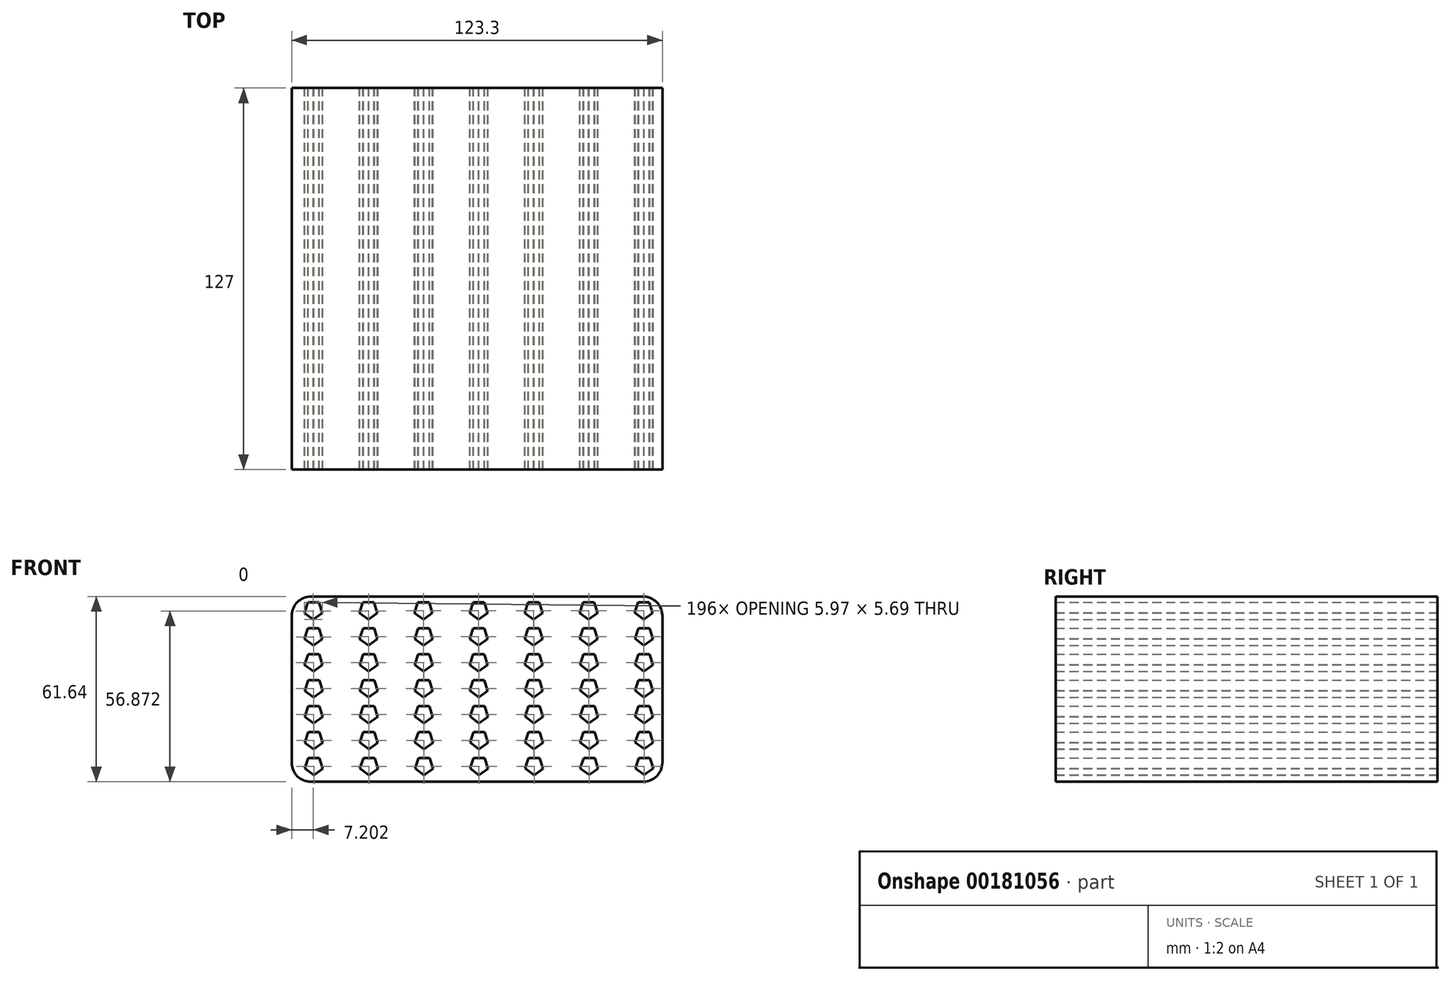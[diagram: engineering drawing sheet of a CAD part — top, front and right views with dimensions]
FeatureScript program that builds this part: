
annotation { "Feature Type Name" : "Feature", "Feature Type Description" : "" }
export const myFeature = defineFeature(function(context is Context, id is Id, definition is map)
    precondition{}
    {
        {
            var Q0;
            Q0=qCreatedBy(makeId("Front.planeOp"),FACE);
            var sketch = newSketch(context, id + "F0", { "sketchPlane" : qUnion([Q0])});
            skLineSegment(sketch, "E0.bottom", {"start": v(55.3, 30.82) * mm, "end": v(-55.3, 30.82) * mm});
            skLineSegment(sketch, "E0.top", {"start": v(55.3, -30.82) * mm, "end": v(-55.3, -30.82) * mm});
            skLineSegment(sketch, "E0.left", {"start": v(61.65, 24.47) * mm, "end": v(61.65, -24.47) * mm});
            skLineSegment(sketch, "E0.right", {"start": v(-61.65, 24.47) * mm, "end": v(-61.65, -24.47) * mm});
            skPoint(sketch, "E0.middle", {"position": v(0, 0) * mm});
            skCircle(sketch, "E1.cCircle", {"center": v(-54.44, 26.35) * mm, "radius": 2.54 * mm, "construction": true});
            skLineSegment(sketch, "E1.0", {"start": v(-52.58, 28.87) * mm, "end": v(-51.46, 25.36) * mm});
            skLineSegment(sketch, "E1.1", {"start": v(-51.46, 25.36) * mm, "end": v(-54.46, 23.2) * mm});
            skLineSegment(sketch, "E1.2", {"start": v(-54.46, 23.2) * mm, "end": v(-57.43, 25.4) * mm});
            skLineSegment(sketch, "E1.3", {"start": v(-57.43, 25.4) * mm, "end": v(-56.27, 28.9) * mm});
            skLineSegment(sketch, "E1.4", {"start": v(-56.27, 28.9) * mm, "end": v(-52.58, 28.87) * mm});
            skPoint(sketch, "E1.0.midPoint", {"position": v(-52.02, 27.12) * mm});
            skPoint(sketch, "E2.0.1.0", {"position": v(-52, 18.49) * mm});
            skLineSegment(sketch, "E2.0.1.1", {"start": v(-56.24, 20.27) * mm, "end": v(-52.55, 20.24) * mm});
            skLineSegment(sketch, "E2.0.1.2", {"start": v(-51.43, 16.73) * mm, "end": v(-54.43, 14.58) * mm});
            skLineSegment(sketch, "E2.0.1.3", {"start": v(-57.4, 16.76) * mm, "end": v(-56.24, 20.27) * mm});
            skLineSegment(sketch, "E2.0.1.4", {"start": v(-54.43, 14.58) * mm, "end": v(-57.4, 16.76) * mm});
            skLineSegment(sketch, "E2.0.1.5", {"start": v(-52.55, 20.24) * mm, "end": v(-51.43, 16.73) * mm});
            skCircle(sketch, "E2.0.1.6", {"center": v(-54.41, 17.72) * mm, "radius": 2.54 * mm, "construction": true});
            skPoint(sketch, "E2.0.2.0", {"position": v(-51.96, 9.86) * mm});
            skLineSegment(sketch, "E2.0.2.1", {"start": v(-56.21, 11.64) * mm, "end": v(-52.52, 11.61) * mm});
            skLineSegment(sketch, "E2.0.2.2", {"start": v(-51.4, 8.1) * mm, "end": v(-54.4, 5.95) * mm});
            skLineSegment(sketch, "E2.0.2.3", {"start": v(-57.37, 8.13) * mm, "end": v(-56.21, 11.64) * mm});
            skLineSegment(sketch, "E2.0.2.4", {"start": v(-54.4, 5.95) * mm, "end": v(-57.37, 8.13) * mm});
            skLineSegment(sketch, "E2.0.2.5", {"start": v(-52.52, 11.61) * mm, "end": v(-51.4, 8.1) * mm});
            skCircle(sketch, "E2.0.2.6", {"center": v(-54.38, 9.09) * mm, "radius": 2.54 * mm, "construction": true});
            skPoint(sketch, "E2.0.3.0", {"position": v(-51.93, 1.23) * mm});
            skLineSegment(sketch, "E2.0.3.1", {"start": v(-56.18, 3) * mm, "end": v(-52.5, 2.98) * mm});
            skLineSegment(sketch, "E2.0.3.2", {"start": v(-51.37, -0.53) * mm, "end": v(-54.37, -2.68) * mm});
            skLineSegment(sketch, "E2.0.3.3", {"start": v(-57.34, -0.5) * mm, "end": v(-56.18, 3) * mm});
            skLineSegment(sketch, "E2.0.3.4", {"start": v(-54.37, -2.68) * mm, "end": v(-57.34, -0.5) * mm});
            skLineSegment(sketch, "E2.0.3.5", {"start": v(-52.5, 2.98) * mm, "end": v(-51.37, -0.53) * mm});
            skCircle(sketch, "E2.0.3.6", {"center": v(-54.35, 0.46) * mm, "radius": 2.54 * mm, "construction": true});
            skPoint(sketch, "E2.0.4.0", {"position": v(-51.9, -7.4) * mm});
            skLineSegment(sketch, "E2.0.4.1", {"start": v(-56.15, -5.62) * mm, "end": v(-52.46, -5.65) * mm});
            skLineSegment(sketch, "E2.0.4.2", {"start": v(-51.34, -9.16) * mm, "end": v(-54.34, -11.31) * mm});
            skLineSegment(sketch, "E2.0.4.3", {"start": v(-57.31, -9.13) * mm, "end": v(-56.15, -5.62) * mm});
            skLineSegment(sketch, "E2.0.4.4", {"start": v(-54.34, -11.31) * mm, "end": v(-57.31, -9.13) * mm});
            skLineSegment(sketch, "E2.0.4.5", {"start": v(-52.46, -5.65) * mm, "end": v(-51.34, -9.16) * mm});
            skCircle(sketch, "E2.0.4.6", {"center": v(-54.32, -8.17) * mm, "radius": 2.54 * mm, "construction": true});
            skPoint(sketch, "E2.0.5.0", {"position": v(-51.87, -16.03) * mm});
            skLineSegment(sketch, "E2.0.5.1", {"start": v(-56.12, -14.25) * mm, "end": v(-52.43, -14.28) * mm});
            skLineSegment(sketch, "E2.0.5.2", {"start": v(-51.31, -17.8) * mm, "end": v(-54.31, -19.94) * mm});
            skLineSegment(sketch, "E2.0.5.3", {"start": v(-57.29, -17.76) * mm, "end": v(-56.12, -14.25) * mm});
            skLineSegment(sketch, "E2.0.5.4", {"start": v(-54.31, -19.94) * mm, "end": v(-57.29, -17.76) * mm});
            skLineSegment(sketch, "E2.0.5.5", {"start": v(-52.43, -14.28) * mm, "end": v(-51.31, -17.8) * mm});
            skCircle(sketch, "E2.0.5.6", {"center": v(-54.3, -16.8) * mm, "radius": 2.54 * mm, "construction": true});
            skPoint(sketch, "E2.0.6.0", {"position": v(-51.84, -24.67) * mm});
            skLineSegment(sketch, "E2.0.6.1", {"start": v(-56.1, -22.88) * mm, "end": v(-52.4, -22.9) * mm});
            skLineSegment(sketch, "E2.0.6.2", {"start": v(-51.28, -26.42) * mm, "end": v(-54.28, -28.57) * mm});
            skLineSegment(sketch, "E2.0.6.3", {"start": v(-57.26, -26.39) * mm, "end": v(-56.1, -22.88) * mm});
            skLineSegment(sketch, "E2.0.6.4", {"start": v(-54.28, -28.57) * mm, "end": v(-57.26, -26.39) * mm});
            skLineSegment(sketch, "E2.0.6.5", {"start": v(-52.4, -22.9) * mm, "end": v(-51.28, -26.42) * mm});
            skCircle(sketch, "E2.0.6.6", {"center": v(-54.26, -25.44) * mm, "radius": 2.54 * mm, "construction": true});
            skPoint(sketch, "E2.1.0.0", {"position": v(-33.7, 27.12) * mm});
            skLineSegment(sketch, "E2.1.0.1", {"start": v(-37.95, 28.9) * mm, "end": v(-34.26, 28.88) * mm});
            skLineSegment(sketch, "E2.1.0.2", {"start": v(-33.14, 25.36) * mm, "end": v(-36.14, 23.21) * mm});
            skLineSegment(sketch, "E2.1.0.3", {"start": v(-39.12, 25.4) * mm, "end": v(-37.95, 28.9) * mm});
            skLineSegment(sketch, "E2.1.0.4", {"start": v(-36.14, 23.21) * mm, "end": v(-39.12, 25.4) * mm});
            skLineSegment(sketch, "E2.1.0.5", {"start": v(-34.26, 28.88) * mm, "end": v(-33.14, 25.36) * mm});
            skCircle(sketch, "E2.1.0.6", {"center": v(-36.12, 26.35) * mm, "radius": 2.54 * mm, "construction": true});
            skPoint(sketch, "E2.1.1.0", {"position": v(-33.67, 18.5) * mm});
            skLineSegment(sketch, "E2.1.1.1", {"start": v(-37.92, 20.27) * mm, "end": v(-34.23, 20.25) * mm});
            skLineSegment(sketch, "E2.1.1.2", {"start": v(-33.11, 16.73) * mm, "end": v(-36.11, 14.58) * mm});
            skLineSegment(sketch, "E2.1.1.3", {"start": v(-39.09, 16.77) * mm, "end": v(-37.92, 20.27) * mm});
            skLineSegment(sketch, "E2.1.1.4", {"start": v(-36.11, 14.58) * mm, "end": v(-39.09, 16.77) * mm});
            skLineSegment(sketch, "E2.1.1.5", {"start": v(-34.23, 20.25) * mm, "end": v(-33.11, 16.73) * mm});
            skCircle(sketch, "E2.1.1.6", {"center": v(-36.1, 17.72) * mm, "radius": 2.54 * mm, "construction": true});
            skPoint(sketch, "E2.1.2.0", {"position": v(-33.64, 9.86) * mm});
            skLineSegment(sketch, "E2.1.2.1", {"start": v(-37.9, 11.64) * mm, "end": v(-34.2, 11.62) * mm});
            skLineSegment(sketch, "E2.1.2.2", {"start": v(-33.08, 8.1) * mm, "end": v(-36.08, 5.95) * mm});
            skLineSegment(sketch, "E2.1.2.3", {"start": v(-39.06, 8.14) * mm, "end": v(-37.9, 11.64) * mm});
            skLineSegment(sketch, "E2.1.2.4", {"start": v(-36.08, 5.95) * mm, "end": v(-39.06, 8.14) * mm});
            skLineSegment(sketch, "E2.1.2.5", {"start": v(-34.2, 11.62) * mm, "end": v(-33.08, 8.1) * mm});
            skCircle(sketch, "E2.1.2.6", {"center": v(-36.06, 9.1) * mm, "radius": 2.54 * mm, "construction": true});
            skPoint(sketch, "E2.1.3.0", {"position": v(-33.61, 1.23) * mm});
            skLineSegment(sketch, "E2.1.3.1", {"start": v(-37.86, 3.01) * mm, "end": v(-34.17, 2.99) * mm});
            skLineSegment(sketch, "E2.1.3.2", {"start": v(-33.06, -0.53) * mm, "end": v(-36.05, -2.68) * mm});
            skLineSegment(sketch, "E2.1.3.3", {"start": v(-39.03, -0.5) * mm, "end": v(-37.86, 3.01) * mm});
            skLineSegment(sketch, "E2.1.3.4", {"start": v(-36.05, -2.68) * mm, "end": v(-39.03, -0.5) * mm});
            skLineSegment(sketch, "E2.1.3.5", {"start": v(-34.17, 2.99) * mm, "end": v(-33.06, -0.53) * mm});
            skCircle(sketch, "E2.1.3.6", {"center": v(-36.04, 0.46) * mm, "radius": 2.54 * mm, "construction": true});
            skPoint(sketch, "E2.1.4.0", {"position": v(-33.58, -7.4) * mm});
            skLineSegment(sketch, "E2.1.4.1", {"start": v(-37.84, -5.62) * mm, "end": v(-34.14, -5.64) * mm});
            skLineSegment(sketch, "E2.1.4.2", {"start": v(-33.03, -9.16) * mm, "end": v(-36.02, -11.3) * mm});
            skLineSegment(sketch, "E2.1.4.3", {"start": v(-39, -9.12) * mm, "end": v(-37.84, -5.62) * mm});
            skLineSegment(sketch, "E2.1.4.4", {"start": v(-36.02, -11.3) * mm, "end": v(-39, -9.12) * mm});
            skLineSegment(sketch, "E2.1.4.5", {"start": v(-34.14, -5.64) * mm, "end": v(-33.03, -9.16) * mm});
            skCircle(sketch, "E2.1.4.6", {"center": v(-36, -8.17) * mm, "radius": 2.54 * mm, "construction": true});
            skPoint(sketch, "E2.1.5.0", {"position": v(-33.56, -16.03) * mm});
            skLineSegment(sketch, "E2.1.5.1", {"start": v(-37.8, -14.25) * mm, "end": v(-34.11, -14.27) * mm});
            skLineSegment(sketch, "E2.1.5.2", {"start": v(-33, -17.79) * mm, "end": v(-36, -19.94) * mm});
            skLineSegment(sketch, "E2.1.5.3", {"start": v(-38.97, -17.75) * mm, "end": v(-37.8, -14.25) * mm});
            skLineSegment(sketch, "E2.1.5.4", {"start": v(-36, -19.94) * mm, "end": v(-38.97, -17.75) * mm});
            skLineSegment(sketch, "E2.1.5.5", {"start": v(-34.11, -14.27) * mm, "end": v(-33, -17.79) * mm});
            skCircle(sketch, "E2.1.5.6", {"center": v(-35.98, -16.8) * mm, "radius": 2.54 * mm, "construction": true});
            skPoint(sketch, "E2.1.6.0", {"position": v(-33.53, -24.66) * mm});
            skLineSegment(sketch, "E2.1.6.1", {"start": v(-37.78, -22.88) * mm, "end": v(-34.09, -22.9) * mm});
            skLineSegment(sketch, "E2.1.6.2", {"start": v(-32.97, -26.42) * mm, "end": v(-35.97, -28.57) * mm});
            skLineSegment(sketch, "E2.1.6.3", {"start": v(-38.94, -26.38) * mm, "end": v(-37.78, -22.88) * mm});
            skLineSegment(sketch, "E2.1.6.4", {"start": v(-35.97, -28.57) * mm, "end": v(-38.94, -26.38) * mm});
            skLineSegment(sketch, "E2.1.6.5", {"start": v(-34.09, -22.9) * mm, "end": v(-32.97, -26.42) * mm});
            skCircle(sketch, "E2.1.6.6", {"center": v(-35.95, -25.43) * mm, "radius": 2.54 * mm, "construction": true});
            skPoint(sketch, "E2.2.0.0", {"position": v(-15.39, 27.13) * mm});
            skLineSegment(sketch, "E2.2.0.1", {"start": v(-19.64, 28.9) * mm, "end": v(-15.95, 28.89) * mm});
            skLineSegment(sketch, "E2.2.0.2", {"start": v(-14.83, 25.37) * mm, "end": v(-17.83, 23.22) * mm});
            skLineSegment(sketch, "E2.2.0.3", {"start": v(-20.8, 25.4) * mm, "end": v(-19.64, 28.9) * mm});
            skLineSegment(sketch, "E2.2.0.4", {"start": v(-17.83, 23.22) * mm, "end": v(-20.8, 25.4) * mm});
            skLineSegment(sketch, "E2.2.0.5", {"start": v(-15.95, 28.89) * mm, "end": v(-14.83, 25.37) * mm});
            skCircle(sketch, "E2.2.0.6", {"center": v(-17.8, 26.36) * mm, "radius": 2.54 * mm, "construction": true});
            skPoint(sketch, "E2.2.1.0", {"position": v(-15.36, 18.5) * mm});
            skLineSegment(sketch, "E2.2.1.1", {"start": v(-19.6, 20.28) * mm, "end": v(-15.92, 20.26) * mm});
            skLineSegment(sketch, "E2.2.1.2", {"start": v(-14.8, 16.74) * mm, "end": v(-17.8, 14.59) * mm});
            skLineSegment(sketch, "E2.2.1.3", {"start": v(-20.77, 16.78) * mm, "end": v(-19.6, 20.28) * mm});
            skLineSegment(sketch, "E2.2.1.4", {"start": v(-17.8, 14.59) * mm, "end": v(-20.77, 16.78) * mm});
            skLineSegment(sketch, "E2.2.1.5", {"start": v(-15.92, 20.26) * mm, "end": v(-14.8, 16.74) * mm});
            skCircle(sketch, "E2.2.1.6", {"center": v(-17.78, 17.73) * mm, "radius": 2.54 * mm, "construction": true});
            skPoint(sketch, "E2.2.2.0", {"position": v(-15.33, 9.87) * mm});
            skLineSegment(sketch, "E2.2.2.1", {"start": v(-19.58, 11.65) * mm, "end": v(-15.89, 11.63) * mm});
            skLineSegment(sketch, "E2.2.2.2", {"start": v(-14.77, 8.1) * mm, "end": v(-17.77, 5.96) * mm});
            skLineSegment(sketch, "E2.2.2.3", {"start": v(-20.74, 8.15) * mm, "end": v(-19.58, 11.65) * mm});
            skLineSegment(sketch, "E2.2.2.4", {"start": v(-17.77, 5.96) * mm, "end": v(-20.74, 8.15) * mm});
            skLineSegment(sketch, "E2.2.2.5", {"start": v(-15.89, 11.63) * mm, "end": v(-14.77, 8.1) * mm});
            skCircle(sketch, "E2.2.2.6", {"center": v(-17.75, 9.1) * mm, "radius": 2.54 * mm, "construction": true});
            skPoint(sketch, "E2.2.3.0", {"position": v(-15.3, 1.24) * mm});
            skLineSegment(sketch, "E2.2.3.1", {"start": v(-19.55, 3.02) * mm, "end": v(-15.86, 3) * mm});
            skLineSegment(sketch, "E2.2.3.2", {"start": v(-14.74, -0.52) * mm, "end": v(-17.74, -2.67) * mm});
            skLineSegment(sketch, "E2.2.3.3", {"start": v(-20.7, -0.48) * mm, "end": v(-19.55, 3.02) * mm});
            skLineSegment(sketch, "E2.2.3.4", {"start": v(-17.74, -2.67) * mm, "end": v(-20.7, -0.48) * mm});
            skLineSegment(sketch, "E2.2.3.5", {"start": v(-15.86, 3) * mm, "end": v(-14.74, -0.52) * mm});
            skCircle(sketch, "E2.2.3.6", {"center": v(-17.72, 0.47) * mm, "radius": 2.54 * mm, "construction": true});
            skPoint(sketch, "E2.2.4.0", {"position": v(-15.27, -7.4) * mm});
            skLineSegment(sketch, "E2.2.4.1", {"start": v(-19.52, -5.61) * mm, "end": v(-15.83, -5.63) * mm});
            skLineSegment(sketch, "E2.2.4.2", {"start": v(-14.7, -9.15) * mm, "end": v(-17.7, -11.3) * mm});
            skLineSegment(sketch, "E2.2.4.3", {"start": v(-20.68, -9.11) * mm, "end": v(-19.52, -5.61) * mm});
            skLineSegment(sketch, "E2.2.4.4", {"start": v(-17.7, -11.3) * mm, "end": v(-20.68, -9.11) * mm});
            skLineSegment(sketch, "E2.2.4.5", {"start": v(-15.83, -5.63) * mm, "end": v(-14.7, -9.15) * mm});
            skCircle(sketch, "E2.2.4.6", {"center": v(-17.69, -8.16) * mm, "radius": 2.54 * mm, "construction": true});
            skPoint(sketch, "E2.2.5.0", {"position": v(-15.24, -16.02) * mm});
            skLineSegment(sketch, "E2.2.5.1", {"start": v(-19.49, -14.24) * mm, "end": v(-15.8, -14.26) * mm});
            skLineSegment(sketch, "E2.2.5.2", {"start": v(-14.68, -17.78) * mm, "end": v(-17.68, -19.93) * mm});
            skLineSegment(sketch, "E2.2.5.3", {"start": v(-20.65, -17.75) * mm, "end": v(-19.49, -14.24) * mm});
            skLineSegment(sketch, "E2.2.5.4", {"start": v(-17.68, -19.93) * mm, "end": v(-20.65, -17.75) * mm});
            skLineSegment(sketch, "E2.2.5.5", {"start": v(-15.8, -14.26) * mm, "end": v(-14.68, -17.78) * mm});
            skCircle(sketch, "E2.2.5.6", {"center": v(-17.66, -16.8) * mm, "radius": 2.54 * mm, "construction": true});
            skPoint(sketch, "E2.2.6.0", {"position": v(-15.2, -24.65) * mm});
            skLineSegment(sketch, "E2.2.6.1", {"start": v(-19.46, -22.87) * mm, "end": v(-15.77, -22.9) * mm});
            skLineSegment(sketch, "E2.2.6.2", {"start": v(-14.65, -26.41) * mm, "end": v(-17.65, -28.56) * mm});
            skLineSegment(sketch, "E2.2.6.3", {"start": v(-20.62, -26.38) * mm, "end": v(-19.46, -22.87) * mm});
            skLineSegment(sketch, "E2.2.6.4", {"start": v(-17.65, -28.56) * mm, "end": v(-20.62, -26.38) * mm});
            skLineSegment(sketch, "E2.2.6.5", {"start": v(-15.77, -22.9) * mm, "end": v(-14.65, -26.41) * mm});
            skCircle(sketch, "E2.2.6.6", {"center": v(-17.63, -25.42) * mm, "radius": 2.54 * mm, "construction": true});
            skPoint(sketch, "E2.3.0.0", {"position": v(2.93, 27.13) * mm});
            skLineSegment(sketch, "E2.3.0.1", {"start": v(-1.32, 28.91) * mm, "end": v(2.37, 28.9) * mm});
            skLineSegment(sketch, "E2.3.0.2", {"start": v(3.5, 25.37) * mm, "end": v(0.5, 23.22) * mm});
            skLineSegment(sketch, "E2.3.0.3", {"start": v(-2.48, 25.41) * mm, "end": v(-1.32, 28.91) * mm});
            skLineSegment(sketch, "E2.3.0.4", {"start": v(0.5, 23.22) * mm, "end": v(-2.48, 25.41) * mm});
            skLineSegment(sketch, "E2.3.0.5", {"start": v(2.37, 28.9) * mm, "end": v(3.5, 25.37) * mm});
            skCircle(sketch, "E2.3.0.6", {"center": v(0.51, 26.36) * mm, "radius": 2.54 * mm, "construction": true});
            skPoint(sketch, "E2.3.1.0", {"position": v(2.96, 18.5) * mm});
            skLineSegment(sketch, "E2.3.1.1", {"start": v(-1.29, 20.28) * mm, "end": v(2.4, 20.26) * mm});
            skLineSegment(sketch, "E2.3.1.2", {"start": v(3.52, 16.74) * mm, "end": v(0.52, 14.6) * mm});
            skLineSegment(sketch, "E2.3.1.3", {"start": v(-2.45, 16.78) * mm, "end": v(-1.29, 20.28) * mm});
            skLineSegment(sketch, "E2.3.1.4", {"start": v(0.52, 14.6) * mm, "end": v(-2.45, 16.78) * mm});
            skLineSegment(sketch, "E2.3.1.5", {"start": v(2.4, 20.26) * mm, "end": v(3.52, 16.74) * mm});
            skCircle(sketch, "E2.3.1.6", {"center": v(0.54, 17.73) * mm, "radius": 2.54 * mm, "construction": true});
            skPoint(sketch, "E2.3.2.0", {"position": v(3, 9.87) * mm});
            skLineSegment(sketch, "E2.3.2.1", {"start": v(-1.26, 11.65) * mm, "end": v(2.43, 11.63) * mm});
            skLineSegment(sketch, "E2.3.2.2", {"start": v(3.55, 8.11) * mm, "end": v(0.55, 5.96) * mm});
            skLineSegment(sketch, "E2.3.2.3", {"start": v(-2.42, 8.15) * mm, "end": v(-1.26, 11.65) * mm});
            skLineSegment(sketch, "E2.3.2.4", {"start": v(0.55, 5.96) * mm, "end": v(-2.42, 8.15) * mm});
            skLineSegment(sketch, "E2.3.2.5", {"start": v(2.43, 11.63) * mm, "end": v(3.55, 8.11) * mm});
            skCircle(sketch, "E2.3.2.6", {"center": v(0.57, 9.1) * mm, "radius": 2.54 * mm, "construction": true});
            skPoint(sketch, "E2.3.3.0", {"position": v(3.02, 1.24) * mm});
            skLineSegment(sketch, "E2.3.3.1", {"start": v(-1.23, 3.02) * mm, "end": v(2.46, 3) * mm});
            skLineSegment(sketch, "E2.3.3.2", {"start": v(3.58, -0.52) * mm, "end": v(0.58, -2.67) * mm});
            skLineSegment(sketch, "E2.3.3.3", {"start": v(-2.4, -0.48) * mm, "end": v(-1.23, 3.02) * mm});
            skLineSegment(sketch, "E2.3.3.4", {"start": v(0.58, -2.67) * mm, "end": v(-2.4, -0.48) * mm});
            skLineSegment(sketch, "E2.3.3.5", {"start": v(2.46, 3) * mm, "end": v(3.58, -0.52) * mm});
            skCircle(sketch, "E2.3.3.6", {"center": v(0.6, 0.47) * mm, "radius": 2.54 * mm, "construction": true});
            skPoint(sketch, "E2.3.4.0", {"position": v(3.05, -7.39) * mm});
            skLineSegment(sketch, "E2.3.4.1", {"start": v(-1.2, -5.6) * mm, "end": v(2.5, -5.63) * mm});
            skLineSegment(sketch, "E2.3.4.2", {"start": v(3.6, -9.15) * mm, "end": v(0.61, -11.3) * mm});
            skLineSegment(sketch, "E2.3.4.3", {"start": v(-2.36, -9.1) * mm, "end": v(-1.2, -5.6) * mm});
            skLineSegment(sketch, "E2.3.4.4", {"start": v(0.61, -11.3) * mm, "end": v(-2.36, -9.1) * mm});
            skLineSegment(sketch, "E2.3.4.5", {"start": v(2.5, -5.63) * mm, "end": v(3.6, -9.15) * mm});
            skCircle(sketch, "E2.3.4.6", {"center": v(0.63, -8.16) * mm, "radius": 2.54 * mm, "construction": true});
            skPoint(sketch, "E2.3.5.0", {"position": v(3.08, -16.02) * mm});
            skLineSegment(sketch, "E2.3.5.1", {"start": v(-1.17, -14.24) * mm, "end": v(2.52, -14.26) * mm});
            skLineSegment(sketch, "E2.3.5.2", {"start": v(3.64, -17.78) * mm, "end": v(0.64, -19.93) * mm});
            skLineSegment(sketch, "E2.3.5.3", {"start": v(-2.33, -17.74) * mm, "end": v(-1.17, -14.24) * mm});
            skLineSegment(sketch, "E2.3.5.4", {"start": v(0.64, -19.93) * mm, "end": v(-2.33, -17.74) * mm});
            skLineSegment(sketch, "E2.3.5.5", {"start": v(2.52, -14.26) * mm, "end": v(3.64, -17.78) * mm});
            skCircle(sketch, "E2.3.5.6", {"center": v(0.66, -16.79) * mm, "radius": 2.54 * mm, "construction": true});
            skPoint(sketch, "E2.3.6.0", {"position": v(3.1, -24.65) * mm});
            skLineSegment(sketch, "E2.3.6.1", {"start": v(-1.14, -22.87) * mm, "end": v(2.55, -22.89) * mm});
            skLineSegment(sketch, "E2.3.6.2", {"start": v(3.67, -26.4) * mm, "end": v(0.67, -28.56) * mm});
            skLineSegment(sketch, "E2.3.6.3", {"start": v(-2.3, -26.37) * mm, "end": v(-1.14, -22.87) * mm});
            skLineSegment(sketch, "E2.3.6.4", {"start": v(0.67, -28.56) * mm, "end": v(-2.3, -26.37) * mm});
            skLineSegment(sketch, "E2.3.6.5", {"start": v(2.55, -22.89) * mm, "end": v(3.67, -26.4) * mm});
            skCircle(sketch, "E2.3.6.6", {"center": v(0.69, -25.42) * mm, "radius": 2.54 * mm, "construction": true});
            skPoint(sketch, "E2.4.0.0", {"position": v(21.25, 27.14) * mm});
            skLineSegment(sketch, "E2.4.0.1", {"start": v(17, 28.92) * mm, "end": v(20.69, 28.9) * mm});
            skLineSegment(sketch, "E2.4.0.2", {"start": v(21.8, 25.38) * mm, "end": v(18.8, 23.23) * mm});
            skLineSegment(sketch, "E2.4.0.3", {"start": v(15.84, 25.42) * mm, "end": v(17, 28.92) * mm});
            skLineSegment(sketch, "E2.4.0.4", {"start": v(18.8, 23.23) * mm, "end": v(15.84, 25.42) * mm});
            skLineSegment(sketch, "E2.4.0.5", {"start": v(20.69, 28.9) * mm, "end": v(21.8, 25.38) * mm});
            skCircle(sketch, "E2.4.0.6", {"center": v(18.83, 26.37) * mm, "radius": 2.54 * mm, "construction": true});
            skPoint(sketch, "E2.4.1.0", {"position": v(21.28, 18.5) * mm});
            skLineSegment(sketch, "E2.4.1.1", {"start": v(17.03, 20.3) * mm, "end": v(20.72, 20.27) * mm});
            skLineSegment(sketch, "E2.4.1.2", {"start": v(21.84, 16.75) * mm, "end": v(18.84, 14.6) * mm});
            skLineSegment(sketch, "E2.4.1.3", {"start": v(15.87, 16.79) * mm, "end": v(17.03, 20.3) * mm});
            skLineSegment(sketch, "E2.4.1.4", {"start": v(18.84, 14.6) * mm, "end": v(15.87, 16.79) * mm});
            skLineSegment(sketch, "E2.4.1.5", {"start": v(20.72, 20.27) * mm, "end": v(21.84, 16.75) * mm});
            skCircle(sketch, "E2.4.1.6", {"center": v(18.86, 17.74) * mm, "radius": 2.54 * mm, "construction": true});
            skPoint(sketch, "E2.4.2.0", {"position": v(21.3, 9.88) * mm});
            skLineSegment(sketch, "E2.4.2.1", {"start": v(17.06, 11.66) * mm, "end": v(20.75, 11.64) * mm});
            skLineSegment(sketch, "E2.4.2.2", {"start": v(21.87, 8.12) * mm, "end": v(18.87, 5.97) * mm});
            skLineSegment(sketch, "E2.4.2.3", {"start": v(15.9, 8.16) * mm, "end": v(17.06, 11.66) * mm});
            skLineSegment(sketch, "E2.4.2.4", {"start": v(18.87, 5.97) * mm, "end": v(15.9, 8.16) * mm});
            skLineSegment(sketch, "E2.4.2.5", {"start": v(20.75, 11.64) * mm, "end": v(21.87, 8.12) * mm});
            skCircle(sketch, "E2.4.2.6", {"center": v(18.89, 9.1) * mm, "radius": 2.54 * mm, "construction": true});
            skPoint(sketch, "E2.4.3.0", {"position": v(21.34, 1.25) * mm});
            skLineSegment(sketch, "E2.4.3.1", {"start": v(17.09, 3.03) * mm, "end": v(20.78, 3) * mm});
            skLineSegment(sketch, "E2.4.3.2", {"start": v(21.9, -0.5) * mm, "end": v(18.9, -2.66) * mm});
            skLineSegment(sketch, "E2.4.3.3", {"start": v(15.93, -0.47) * mm, "end": v(17.09, 3.03) * mm});
            skLineSegment(sketch, "E2.4.3.4", {"start": v(18.9, -2.66) * mm, "end": v(15.93, -0.47) * mm});
            skLineSegment(sketch, "E2.4.3.5", {"start": v(20.78, 3) * mm, "end": v(21.9, -0.5) * mm});
            skCircle(sketch, "E2.4.3.6", {"center": v(18.92, 0.48) * mm, "radius": 2.54 * mm, "construction": true});
            skPoint(sketch, "E2.4.4.0", {"position": v(21.37, -7.38) * mm});
            skLineSegment(sketch, "E2.4.4.1", {"start": v(17.12, -5.6) * mm, "end": v(20.8, -5.62) * mm});
            skLineSegment(sketch, "E2.4.4.2", {"start": v(21.93, -9.14) * mm, "end": v(18.93, -11.3) * mm});
            skLineSegment(sketch, "E2.4.4.3", {"start": v(15.96, -9.1) * mm, "end": v(17.12, -5.6) * mm});
            skLineSegment(sketch, "E2.4.4.4", {"start": v(18.93, -11.3) * mm, "end": v(15.96, -9.1) * mm});
            skLineSegment(sketch, "E2.4.4.5", {"start": v(20.8, -5.62) * mm, "end": v(21.93, -9.14) * mm});
            skCircle(sketch, "E2.4.4.6", {"center": v(18.95, -8.15) * mm, "radius": 2.54 * mm, "construction": true});
            skPoint(sketch, "E2.4.5.0", {"position": v(21.4, -16.01) * mm});
            skLineSegment(sketch, "E2.4.5.1", {"start": v(17.15, -14.23) * mm, "end": v(20.84, -14.25) * mm});
            skLineSegment(sketch, "E2.4.5.2", {"start": v(21.96, -17.77) * mm, "end": v(18.96, -19.92) * mm});
            skLineSegment(sketch, "E2.4.5.3", {"start": v(15.99, -17.73) * mm, "end": v(17.15, -14.23) * mm});
            skLineSegment(sketch, "E2.4.5.4", {"start": v(18.96, -19.92) * mm, "end": v(15.99, -17.73) * mm});
            skLineSegment(sketch, "E2.4.5.5", {"start": v(20.84, -14.25) * mm, "end": v(21.96, -17.77) * mm});
            skCircle(sketch, "E2.4.5.6", {"center": v(18.98, -16.78) * mm, "radius": 2.54 * mm, "construction": true});
            skPoint(sketch, "E2.4.6.0", {"position": v(21.43, -24.64) * mm});
            skLineSegment(sketch, "E2.4.6.1", {"start": v(17.18, -22.86) * mm, "end": v(20.87, -22.88) * mm});
            skLineSegment(sketch, "E2.4.6.2", {"start": v(21.99, -26.4) * mm, "end": v(18.99, -28.55) * mm});
            skLineSegment(sketch, "E2.4.6.3", {"start": v(16.02, -26.36) * mm, "end": v(17.18, -22.86) * mm});
            skLineSegment(sketch, "E2.4.6.4", {"start": v(18.99, -28.55) * mm, "end": v(16.02, -26.36) * mm});
            skLineSegment(sketch, "E2.4.6.5", {"start": v(20.87, -22.88) * mm, "end": v(21.99, -26.4) * mm});
            skCircle(sketch, "E2.4.6.6", {"center": v(19, -25.41) * mm, "radius": 2.54 * mm, "construction": true});
            skPoint(sketch, "E2.5.0.0", {"position": v(39.57, 27.15) * mm});
            skLineSegment(sketch, "E2.5.0.1", {"start": v(35.32, 28.93) * mm, "end": v(39, 28.9) * mm});
            skLineSegment(sketch, "E2.5.0.2", {"start": v(40.13, 25.39) * mm, "end": v(37.13, 23.24) * mm});
            skLineSegment(sketch, "E2.5.0.3", {"start": v(34.15, 25.42) * mm, "end": v(35.32, 28.93) * mm});
            skLineSegment(sketch, "E2.5.0.4", {"start": v(37.13, 23.24) * mm, "end": v(34.15, 25.42) * mm});
            skLineSegment(sketch, "E2.5.0.5", {"start": v(39, 28.9) * mm, "end": v(40.13, 25.39) * mm});
            skCircle(sketch, "E2.5.0.6", {"center": v(37.15, 26.38) * mm, "radius": 2.54 * mm, "construction": true});
            skPoint(sketch, "E2.5.1.0", {"position": v(39.6, 18.51) * mm});
            skLineSegment(sketch, "E2.5.1.1", {"start": v(35.35, 20.3) * mm, "end": v(39.04, 20.27) * mm});
            skLineSegment(sketch, "E2.5.1.2", {"start": v(40.16, 16.76) * mm, "end": v(37.16, 14.6) * mm});
            skLineSegment(sketch, "E2.5.1.3", {"start": v(34.18, 16.8) * mm, "end": v(35.35, 20.3) * mm});
            skLineSegment(sketch, "E2.5.1.4", {"start": v(37.16, 14.6) * mm, "end": v(34.18, 16.8) * mm});
            skLineSegment(sketch, "E2.5.1.5", {"start": v(39.04, 20.27) * mm, "end": v(40.16, 16.76) * mm});
            skCircle(sketch, "E2.5.1.6", {"center": v(37.18, 17.74) * mm, "radius": 2.54 * mm, "construction": true});
            skPoint(sketch, "E2.5.2.0", {"position": v(39.63, 9.88) * mm});
            skLineSegment(sketch, "E2.5.2.1", {"start": v(35.38, 11.67) * mm, "end": v(39.07, 11.64) * mm});
            skLineSegment(sketch, "E2.5.2.2", {"start": v(40.19, 8.13) * mm, "end": v(37.19, 5.98) * mm});
            skLineSegment(sketch, "E2.5.2.3", {"start": v(34.21, 8.16) * mm, "end": v(35.38, 11.67) * mm});
            skLineSegment(sketch, "E2.5.2.4", {"start": v(37.19, 5.98) * mm, "end": v(34.21, 8.16) * mm});
            skLineSegment(sketch, "E2.5.2.5", {"start": v(39.07, 11.64) * mm, "end": v(40.19, 8.13) * mm});
            skCircle(sketch, "E2.5.2.6", {"center": v(37.2, 9.11) * mm, "radius": 2.54 * mm, "construction": true});
            skPoint(sketch, "E2.5.3.0", {"position": v(39.66, 1.25) * mm});
            skLineSegment(sketch, "E2.5.3.1", {"start": v(35.4, 3.04) * mm, "end": v(39.1, 3.01) * mm});
            skLineSegment(sketch, "E2.5.3.2", {"start": v(40.22, -0.5) * mm, "end": v(37.22, -2.65) * mm});
            skLineSegment(sketch, "E2.5.3.3", {"start": v(34.24, -0.47) * mm, "end": v(35.4, 3.04) * mm});
            skLineSegment(sketch, "E2.5.3.4", {"start": v(37.22, -2.65) * mm, "end": v(34.24, -0.47) * mm});
            skLineSegment(sketch, "E2.5.3.5", {"start": v(39.1, 3.01) * mm, "end": v(40.22, -0.5) * mm});
            skCircle(sketch, "E2.5.3.6", {"center": v(37.24, 0.48) * mm, "radius": 2.54 * mm, "construction": true});
            skPoint(sketch, "E2.5.4.0", {"position": v(39.69, -7.38) * mm});
            skLineSegment(sketch, "E2.5.4.1", {"start": v(35.44, -5.6) * mm, "end": v(39.13, -5.62) * mm});
            skLineSegment(sketch, "E2.5.4.2", {"start": v(40.25, -9.13) * mm, "end": v(37.25, -11.29) * mm});
            skLineSegment(sketch, "E2.5.4.3", {"start": v(34.27, -9.1) * mm, "end": v(35.44, -5.6) * mm});
            skLineSegment(sketch, "E2.5.4.4", {"start": v(37.25, -11.29) * mm, "end": v(34.27, -9.1) * mm});
            skLineSegment(sketch, "E2.5.4.5", {"start": v(39.13, -5.62) * mm, "end": v(40.25, -9.13) * mm});
            skCircle(sketch, "E2.5.4.6", {"center": v(37.27, -8.15) * mm, "radius": 2.54 * mm, "construction": true});
            skPoint(sketch, "E2.5.5.0", {"position": v(39.72, -16) * mm});
            skLineSegment(sketch, "E2.5.5.1", {"start": v(35.47, -14.22) * mm, "end": v(39.16, -14.25) * mm});
            skLineSegment(sketch, "E2.5.5.2", {"start": v(40.27, -17.76) * mm, "end": v(37.28, -19.92) * mm});
            skLineSegment(sketch, "E2.5.5.3", {"start": v(34.3, -17.73) * mm, "end": v(35.47, -14.22) * mm});
            skLineSegment(sketch, "E2.5.5.4", {"start": v(37.28, -19.92) * mm, "end": v(34.3, -17.73) * mm});
            skLineSegment(sketch, "E2.5.5.5", {"start": v(39.16, -14.25) * mm, "end": v(40.27, -17.76) * mm});
            skCircle(sketch, "E2.5.5.6", {"center": v(37.3, -16.78) * mm, "radius": 2.54 * mm, "construction": true});
            skPoint(sketch, "E2.5.6.0", {"position": v(39.75, -24.64) * mm});
            skLineSegment(sketch, "E2.5.6.1", {"start": v(35.5, -22.85) * mm, "end": v(39.19, -22.88) * mm});
            skLineSegment(sketch, "E2.5.6.2", {"start": v(40.3, -26.4) * mm, "end": v(37.3, -28.55) * mm});
            skLineSegment(sketch, "E2.5.6.3", {"start": v(34.33, -26.36) * mm, "end": v(35.5, -22.85) * mm});
            skLineSegment(sketch, "E2.5.6.4", {"start": v(37.3, -28.55) * mm, "end": v(34.33, -26.36) * mm});
            skLineSegment(sketch, "E2.5.6.5", {"start": v(39.19, -22.88) * mm, "end": v(40.3, -26.4) * mm});
            skCircle(sketch, "E2.5.6.6", {"center": v(37.32, -25.4) * mm, "radius": 2.54 * mm, "construction": true});
            skPoint(sketch, "E2.6.0.0", {"position": v(57.88, 27.15) * mm});
            skLineSegment(sketch, "E2.6.0.1", {"start": v(53.63, 28.93) * mm, "end": v(57.33, 28.9) * mm});
            skLineSegment(sketch, "E2.6.0.2", {"start": v(58.44, 25.4) * mm, "end": v(55.44, 23.24) * mm});
            skLineSegment(sketch, "E2.6.0.3", {"start": v(52.47, 25.43) * mm, "end": v(53.63, 28.93) * mm});
            skLineSegment(sketch, "E2.6.0.4", {"start": v(55.44, 23.24) * mm, "end": v(52.47, 25.43) * mm});
            skLineSegment(sketch, "E2.6.0.5", {"start": v(57.33, 28.9) * mm, "end": v(58.44, 25.4) * mm});
            skCircle(sketch, "E2.6.0.6", {"center": v(55.46, 26.38) * mm, "radius": 2.54 * mm, "construction": true});
            skPoint(sketch, "E2.6.1.0", {"position": v(57.91, 18.52) * mm});
            skLineSegment(sketch, "E2.6.1.1", {"start": v(53.66, 20.3) * mm, "end": v(57.35, 20.28) * mm});
            skLineSegment(sketch, "E2.6.1.2", {"start": v(58.47, 16.76) * mm, "end": v(55.47, 14.61) * mm});
            skLineSegment(sketch, "E2.6.1.3", {"start": v(52.5, 16.8) * mm, "end": v(53.66, 20.3) * mm});
            skLineSegment(sketch, "E2.6.1.4", {"start": v(55.47, 14.61) * mm, "end": v(52.5, 16.8) * mm});
            skLineSegment(sketch, "E2.6.1.5", {"start": v(57.35, 20.28) * mm, "end": v(58.47, 16.76) * mm});
            skCircle(sketch, "E2.6.1.6", {"center": v(55.5, 17.75) * mm, "radius": 2.54 * mm, "construction": true});
            skPoint(sketch, "E2.6.2.0", {"position": v(57.94, 9.9) * mm});
            skLineSegment(sketch, "E2.6.2.1", {"start": v(53.7, 11.67) * mm, "end": v(57.38, 11.65) * mm});
            skLineSegment(sketch, "E2.6.2.2", {"start": v(58.5, 8.13) * mm, "end": v(55.5, 5.98) * mm});
            skLineSegment(sketch, "E2.6.2.3", {"start": v(52.53, 8.17) * mm, "end": v(53.7, 11.67) * mm});
            skLineSegment(sketch, "E2.6.2.4", {"start": v(55.5, 5.98) * mm, "end": v(52.53, 8.17) * mm});
            skLineSegment(sketch, "E2.6.2.5", {"start": v(57.38, 11.65) * mm, "end": v(58.5, 8.13) * mm});
            skCircle(sketch, "E2.6.2.6", {"center": v(55.52, 9.12) * mm, "radius": 2.54 * mm, "construction": true});
            skPoint(sketch, "E2.6.3.0", {"position": v(57.97, 1.26) * mm});
            skLineSegment(sketch, "E2.6.3.1", {"start": v(53.72, 3.04) * mm, "end": v(57.41, 3.02) * mm});
            skLineSegment(sketch, "E2.6.3.2", {"start": v(58.53, -0.5) * mm, "end": v(55.53, -2.65) * mm});
            skLineSegment(sketch, "E2.6.3.3", {"start": v(52.56, -0.46) * mm, "end": v(53.72, 3.04) * mm});
            skLineSegment(sketch, "E2.6.3.4", {"start": v(55.53, -2.65) * mm, "end": v(52.56, -0.46) * mm});
            skLineSegment(sketch, "E2.6.3.5", {"start": v(57.41, 3.02) * mm, "end": v(58.53, -0.5) * mm});
            skCircle(sketch, "E2.6.3.6", {"center": v(55.55, 0.5) * mm, "radius": 2.54 * mm, "construction": true});
            skPoint(sketch, "E2.6.4.0", {"position": v(58, -7.37) * mm});
            skLineSegment(sketch, "E2.6.4.1", {"start": v(53.75, -5.59) * mm, "end": v(57.44, -5.61) * mm});
            skLineSegment(sketch, "E2.6.4.2", {"start": v(58.56, -9.13) * mm, "end": v(55.56, -11.28) * mm});
            skLineSegment(sketch, "E2.6.4.3", {"start": v(52.6, -9.1) * mm, "end": v(53.75, -5.59) * mm});
            skLineSegment(sketch, "E2.6.4.4", {"start": v(55.56, -11.28) * mm, "end": v(52.6, -9.1) * mm});
            skLineSegment(sketch, "E2.6.4.5", {"start": v(57.44, -5.61) * mm, "end": v(58.56, -9.13) * mm});
            skCircle(sketch, "E2.6.4.6", {"center": v(55.58, -8.14) * mm, "radius": 2.54 * mm, "construction": true});
            skPoint(sketch, "E2.6.5.0", {"position": v(58.03, -16) * mm});
            skLineSegment(sketch, "E2.6.5.1", {"start": v(53.78, -14.22) * mm, "end": v(57.47, -14.24) * mm});
            skLineSegment(sketch, "E2.6.5.2", {"start": v(58.6, -17.76) * mm, "end": v(55.6, -19.9) * mm});
            skLineSegment(sketch, "E2.6.5.3", {"start": v(52.62, -17.72) * mm, "end": v(53.78, -14.22) * mm});
            skLineSegment(sketch, "E2.6.5.4", {"start": v(55.6, -19.9) * mm, "end": v(52.62, -17.72) * mm});
            skLineSegment(sketch, "E2.6.5.5", {"start": v(57.47, -14.24) * mm, "end": v(58.6, -17.76) * mm});
            skCircle(sketch, "E2.6.5.6", {"center": v(55.61, -16.77) * mm, "radius": 2.54 * mm, "construction": true});
            skPoint(sketch, "E2.6.6.0", {"position": v(58.06, -24.63) * mm});
            skLineSegment(sketch, "E2.6.6.1", {"start": v(53.81, -22.85) * mm, "end": v(57.5, -22.87) * mm});
            skLineSegment(sketch, "E2.6.6.2", {"start": v(58.62, -26.39) * mm, "end": v(55.62, -28.54) * mm});
            skLineSegment(sketch, "E2.6.6.3", {"start": v(52.65, -26.35) * mm, "end": v(53.81, -22.85) * mm});
            skLineSegment(sketch, "E2.6.6.4", {"start": v(55.62, -28.54) * mm, "end": v(52.65, -26.35) * mm});
            skLineSegment(sketch, "E2.6.6.5", {"start": v(57.5, -22.87) * mm, "end": v(58.62, -26.39) * mm});
            skCircle(sketch, "E2.6.6.6", {"center": v(55.64, -25.4) * mm, "radius": 2.54 * mm, "construction": true});
            skLineSegment(sketch, "E2.direction1", {"start": v(-57.43, 25.4) * mm, "end": v(-39.12, 25.4) * mm, "construction": true});
            skLineSegment(sketch, "E2.direction2", {"start": v(-57.43, 25.4) * mm, "end": v(-57.4, 16.76) * mm, "construction": true});
            skPoint(sketch, "E3.visualSharp", {"position": v(61.65, 30.82) * mm});
            skArc(sketch, "E3.filletArc", {"start": v(61.65, 24.47) * mm, "mid": v(59.79, 28.96) * mm, "end": v(55.3, 30.82) * mm});
            skPoint(sketch, "E4.visualSharp", {"position": v(61.65, -30.82) * mm});
            skArc(sketch, "E4.filletArc", {"start": v(55.3, -30.82) * mm, "mid": v(59.79, -28.96) * mm, "end": v(61.65, -24.47) * mm});
            skPoint(sketch, "E5.visualSharp", {"position": v(-61.65, -30.82) * mm});
            skArc(sketch, "E5.filletArc", {"start": v(-61.65, -24.47) * mm, "mid": v(-59.79, -28.96) * mm, "end": v(-55.3, -30.82) * mm});
            skPoint(sketch, "E6.visualSharp", {"position": v(-61.65, 30.82) * mm});
            skArc(sketch, "E6.filletArc", {"start": v(-55.3, 30.82) * mm, "mid": v(-59.79, 28.96) * mm, "end": v(-61.65, 24.47) * mm});
            skSolve(sketch);
        }
        {
            var Q0;
            Q0 = qSketchRegion(id + "FBgieGYIDDwo0sN_1", true);
            var Q1;
            Q1=makeQuery(id+"F0.imprint","IMPRINT",FACE,{"disambiguationData":[TD([[makeQuery(id+"F0.imprint","IMPRINT",EDGE,{"derivedFrom":sQuery(id+"F0.wireOp",EDGE,"E0.bottom")}),1.0]])]});
            extrude(context, id + "F1", {"entities" : qUnion([Q0, Q1]), "depth" : 127 * mm});
        }
    });
